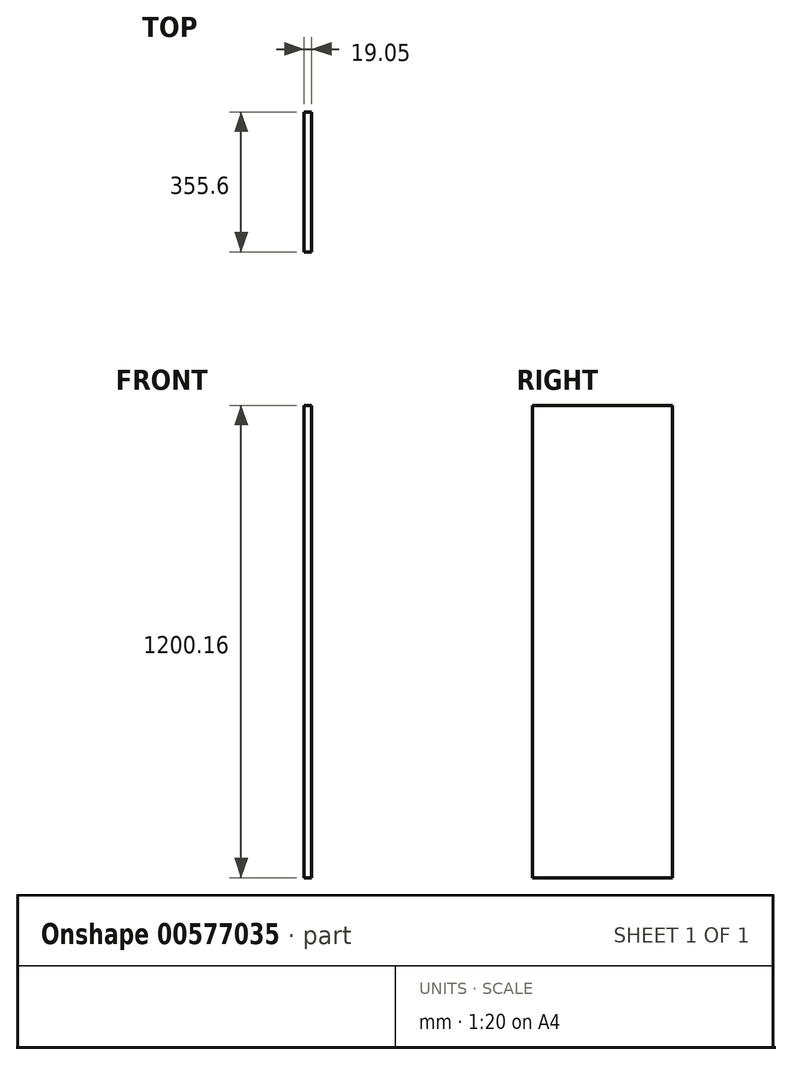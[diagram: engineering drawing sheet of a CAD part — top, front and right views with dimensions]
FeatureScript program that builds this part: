
annotation { "Feature Type Name" : "Feature", "Feature Type Description" : "" }
export const myFeature = defineFeature(function(context is Context, id is Id, definition is map)
    precondition{}
    {
        {
            var Q0;
            Q0=qCreatedBy(makeId("Right.planeOp"),FACE);
            var sketch = newSketch(context, id + "F0", { "sketchPlane" : qUnion([Q0])});
            skLineSegment(sketch, "E0.bottom", {"start": v(177.8, 600.08) * mm, "end": v(-177.8, 600.08) * mm});
            skLineSegment(sketch, "E0.top", {"start": v(177.8, -600.07) * mm, "end": v(-177.8, -600.07) * mm});
            skLineSegment(sketch, "E0.left", {"start": v(177.8, 600.07) * mm, "end": v(177.8, -600.07) * mm});
            skLineSegment(sketch, "E0.right", {"start": v(-177.8, 600.07) * mm, "end": v(-177.8, -600.07) * mm});
            skPoint(sketch, "E0.middle", {"position": v(0, 0) * mm});
            skSolve(sketch);
        }
        {
            var Q0;
            Q0=makeQuery(id+"F0.imprint","IMPRINT",FACE,{"disambiguationData":[TD([[makeQuery(id+"F0.imprint","IMPRINT",EDGE,{"derivedFrom":sQuery(id+"F0.wireOp",EDGE,"E0.bottom")}),1.0]])]});
            extrude(context, id + "F1", {"entities" : qUnion([Q0]), "depth" : 19.05 * mm, "offsetDistance" : 25.4 * mm});
        }
    });
